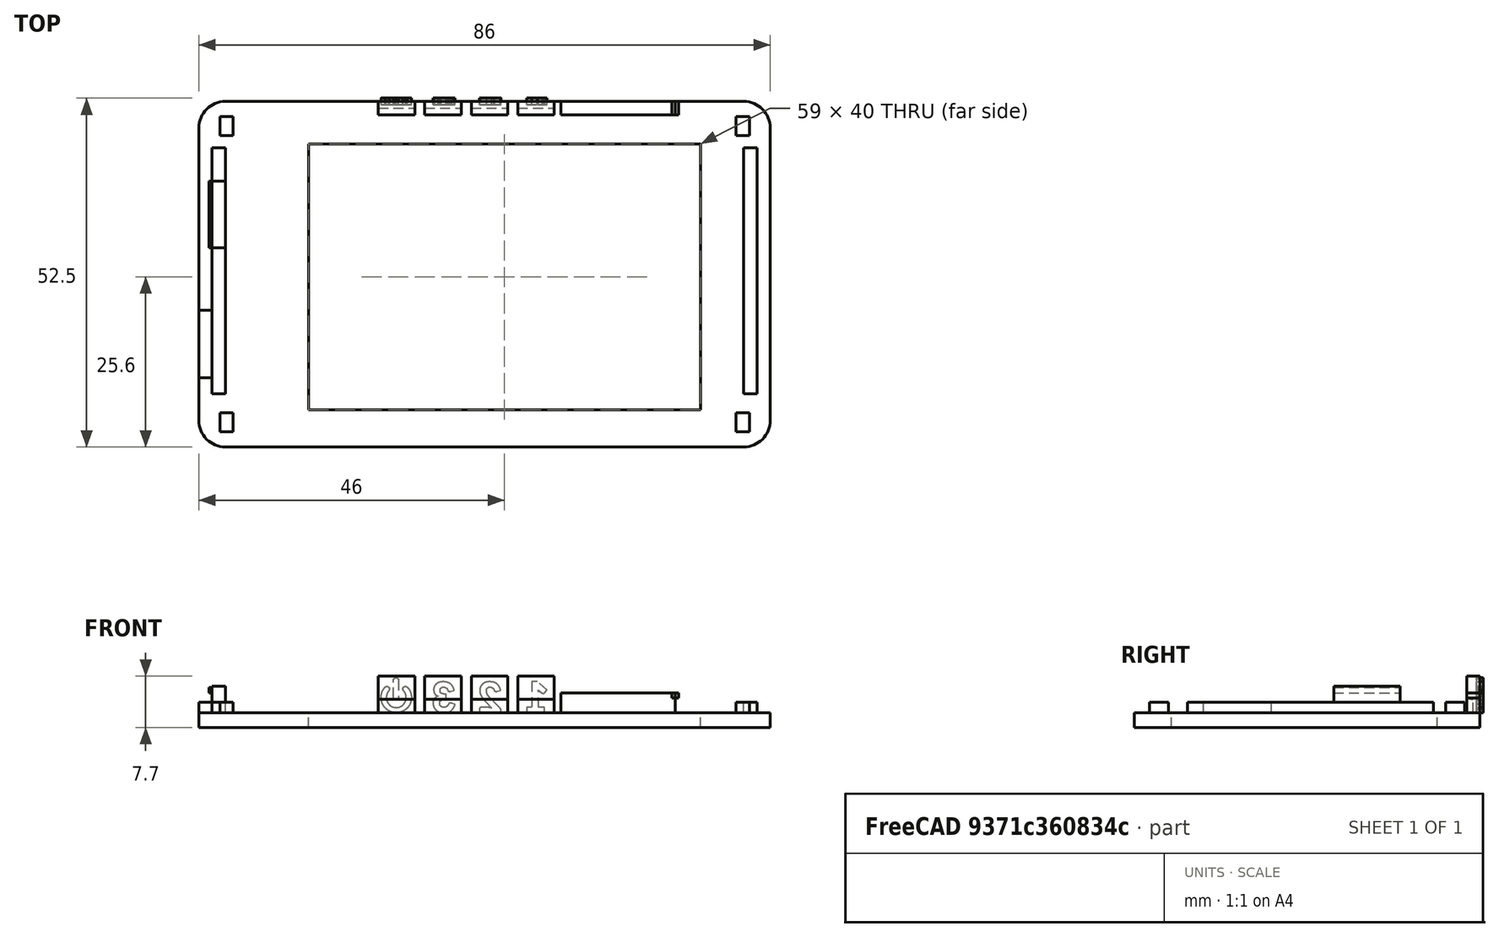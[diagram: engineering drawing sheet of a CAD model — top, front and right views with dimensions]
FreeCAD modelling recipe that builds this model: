
FCSTD DOCUMENT  (FreeCAD 0.18R4 (GitTag))
Label: Lid V4
License: All rights reserved
LicenseURL: http://en.wikipedia.org/wiki/All_rights_reserved
objects: Part::Box×21, Part::Fillet×5, Part::Cut×5, Part::Part2DObjectPython×4, Part::Extrusion×4, Mesh::Feature×1
note: 39 computed .brp shape members not serialized (recipe doc carries the construction recipe); baked Part::Feature solids carry a one-line shape summary decoded from their .brp

FEATURE [Mesh::Feature] TTGO_T5s_hanger___lid_6  label="TTGO_T5s_hanger_-_lid_6"
FEATURE [Part::Box] Box002  label="Würfel002"
  AttacherType = Attacher::AttachEngine3D
  Height = 2.2
  Length = 86
  Placement = pos=(-43,-26,-17.2) rot=(0,0,1;0rad)
  Width = 52
FEATURE [Part::Fillet] Fillet
  Base = -> Box002
  Edges = 4 edges r=4: [Edge1,Edge3,Edge5,Edge7]
FEATURE [Part::Box] Box  label="Würfel"
  AttacherType = Attacher::AttachEngine3D
  Height = 1.6
  Length = 2
  Placement = pos=(39,-18,-15) rot=(0,0,1;0rad)
  Width = 37
FEATURE [Part::Box] Box003  label="Würfel003"
  AttacherType = Attacher::AttachEngine3D
  Height = 1.6
  Length = 2
  Placement = pos=(-41,-18,-15) rot=(0,0,1;0rad)
  Width = 37
FEATURE [Part::Box] Box004  label="Würfel Cliphole"
  AttacherType = Attacher::AttachEngine3D
  Height = 2.4
  Length = 2
  Placement = pos=(-41,4,-13.4) rot=(0,0,1;0rad)
  Width = 10
FEATURE [Part::Box] Box005  label="Würfel USB"
  AttacherType = Attacher::AttachEngine3D
  Height = 1.6
  Length = 2
  Placement = pos=(-43,-15.6,-15) rot=(0,0,1;0rad)
  Width = 10.2
FEATURE [Part::Box] Box010  label="Cliphole"
  AttacherType = Attacher::AttachEngine3D
  Height = 0.8
  Length = 0.5
  Placement = pos=(-41.5,4,-12) rot=(0,0,1;0rad)
  Width = 10
FEATURE [Part::Box] Box011  label="Würfel SD"
  AttacherType = Attacher::AttachEngine3D
  Height = 3
  Length = 17.2
  Placement = pos=(11.5,24,-15) rot=(0,0,1;0rad)
  Width = 2
FEATURE [Part::Box] Box012  label="Würfel Placeholder 1"
  AttacherType = Attacher::AttachEngine3D
  Height = 1.6
  Length = 2
  Placement = pos=(37.85,20.85,-15) rot=(0,0,1;0rad)
  Width = 2.85
FEATURE [Part::Box] Box013  label="Würfel Placeholder 2"
  AttacherType = Attacher::AttachEngine3D
  Height = 1.6
  Length = 2
  Placement = pos=(-39.85,20.85,-15) rot=(0,0,1;0rad)
  Width = 2.85
FEATURE [Part::Box] Box014  label="Würfel Placeholder 3"
  AttacherType = Attacher::AttachEngine3D
  Height = 1.6
  Length = 2
  Placement = pos=(37.85,-23.7,-15) rot=(0,0,1;0rad)
  Width = 2.85
FEATURE [Part::Box] Box015  label="Würfel Placeholder 4"
  AttacherType = Attacher::AttachEngine3D
  Height = 1.6
  Length = 2
  Placement = pos=(-39.85,-23.7,-15) rot=(0,0,1;0rad)
  Width = 2.85
FEATURE [Part::Box] Box016  label="Button 1 Base"
  AttacherType = Attacher::AttachEngine3D
  Height = 5.5
  Length = 5.5
  Placement = pos=(5,24,-15) rot=(0,0,1;0rad)
  Width = 2
FEATURE [Part::Box] Box017  label="Button 1 Cut"
  AttacherType = Attacher::AttachEngine3D
  Height = 2
  Length = 5.5
  Placement = pos=(5,24,-15) rot=(0,0,1;0rad)
  Width = 1
FEATURE [Part::Cut] Cut
  Base = -> Box016
  Tool = -> Box017
FEATURE [Part::Fillet] Fillet002  label="Button 1"
  Base = -> Cut
  Edges = 1 edges r=0.9: [Edge7]
FEATURE [Part::Box] Box018  label="Button 1 Base001"
  AttacherType = Attacher::AttachEngine3D
  Height = 5.5
  Length = 5.5
  Placement = pos=(5,24,-15) rot=(0,0,1;0rad)
  Width = 2
FEATURE [Part::Box] Box019  label="Button 1 Cut001"
  AttacherType = Attacher::AttachEngine3D
  Height = 2
  Length = 5.5
  Placement = pos=(5,24,-15) rot=(0,0,1;0rad)
  Width = 1
FEATURE [Part::Cut] Cut001
  Base = -> Box018
  Tool = -> Box019
FEATURE [Part::Fillet] Fillet003  label="Button 2"
  Base = -> Cut001
  Edges = 1 edges r=0.9: [Edge7]
  Placement = pos=(-7,0,0) rot=(0,0,1;0rad)
FEATURE [Part::Box] Box020  label="Button 1 Base002"
  AttacherType = Attacher::AttachEngine3D
  Height = 5.5
  Length = 5.5
  Placement = pos=(5,24,-15) rot=(0,0,1;0rad)
  Width = 2
FEATURE [Part::Box] Box021  label="Button 1 Cut002"
  AttacherType = Attacher::AttachEngine3D
  Height = 2
  Length = 5.5
  Placement = pos=(5,24,-15) rot=(0,0,1;0rad)
  Width = 1
FEATURE [Part::Cut] Cut002
  Base = -> Box020
  Tool = -> Box021
FEATURE [Part::Fillet] Fillet004  label="Button 3"
  Base = -> Cut002
  Edges = 1 edges r=0.9: [Edge7]
  Placement = pos=(-14,0,0) rot=(0,0,1;0rad)
FEATURE [Part::Box] Box022  label="Button 1 Base003"
  AttacherType = Attacher::AttachEngine3D
  Height = 5.5
  Length = 5.5
  Placement = pos=(5,24,-15) rot=(0,0,1;0rad)
  Width = 2
FEATURE [Part::Box] Box023  label="Button 1 Cut003"
  AttacherType = Attacher::AttachEngine3D
  Height = 2
  Length = 5.5
  Placement = pos=(5,24,-15) rot=(0,0,1;0rad)
  Width = 1
FEATURE [Part::Cut] Cut003
  Base = -> Box022
  Tool = -> Box023
FEATURE [Part::Fillet] Fillet005  label="Button 4"
  Base = -> Cut003
  Edges = 1 edges r=0.9: [Edge7]
  Placement = pos=(-21,0,0) rot=(0,0,1;0rad)
FEATURE [Part::Box] Box024  label="Display Cut"
  AttacherType = Attacher::AttachEngine3D
  Height = 4
  Length = 59
  Placement = pos=(-26.5,-20.4,-18) rot=(0,0,1;0rad)
  Width = 40
FEATURE [Part::Part2DObjectPython] ShapeString  # Draft 2D object (typed FeaturePython)
  FontFile = <userpath>/Documents/3D Printer/All Fonts/Lato-Black.ttf
  Placement = pos=(0,0,0) rot=(0,0.707107,0.707107;3.14159rad)
  Size = 5
  String = 1
  Tracking = 0
FEATURE [Part::Extrusion] Extrude  label="Btn1 Extrude"
  Base = -> ShapeString
  Dir = (0,1,-2e-16)
  DirMode = 2
  FaceMakerClass = Part::FaceMakerBullseye
  LengthFwd = 1
  LengthRev = 0
  Placement = pos=(9.8,25.5,-15) rot=(0,0,1;0rad)
  Solid = false
  Symmetric = false
FEATURE [Part::Part2DObjectPython] ShapeString001  # Draft 2D object (typed FeaturePython)
  FontFile = <userpath>/Documents/3D Printer/All Fonts/Lato-Black.ttf
  Placement = pos=(0,0,0) rot=(0,0.707107,0.707107;3.14159rad)
  Size = 5
  String = 2
  Tracking = 0
FEATURE [Part::Extrusion] Extrude001  label="Btn2 Extrude"
  Base = -> ShapeString001
  Dir = (0,1,-2e-16)
  DirMode = 2
  FaceMakerClass = Part::FaceMakerBullseye
  LengthFwd = 1
  LengthRev = 0
  Placement = pos=(2.7,25.5,-15) rot=(0,0,1;0rad)
  Solid = false
  Symmetric = false
FEATURE [Part::Part2DObjectPython] ShapeString002  # Draft 2D object (typed FeaturePython)
  FontFile = <userpath>/Documents/3D Printer/All Fonts/Lato-Black.ttf
  Placement = pos=(0,0,0) rot=(0,0.707107,0.707107;3.14159rad)
  Size = 5
  String = 3
  Tracking = 0
FEATURE [Part::Extrusion] Extrude002  label="Btn3 Extrude"
  Base = -> ShapeString002
  Dir = (0,1,-2e-16)
  DirMode = 2
  FaceMakerClass = Part::FaceMakerBullseye
  LengthFwd = 1
  LengthRev = 0
  Placement = pos=(-4.2,25.5,-15) rot=(0,0,1;0rad)
  Solid = false
  Symmetric = false
FEATURE [Part::Part2DObjectPython] ShapeString003  # Draft 2D object (typed FeaturePython)
  FontFile = <userpath>/Documents/3D Printer/All Fonts/Unicode_IEC_symbol.ttf
  Placement = pos=(0,0,0) rot=(0,0.707107,0.707107;3.14159rad)
  Size = 4
  String = ⏻
  Tracking = 0
FEATURE [Part::Extrusion] Extrude003  label="Btn4 Extrude"
  Base = -> ShapeString003
  Dir = (0,1,-2e-16)
  DirMode = 2
  FaceMakerClass = Part::FaceMakerBullseye
  LengthFwd = 1
  LengthRev = 0
  Placement = pos=(-10.65,25.5,-15) rot=(0,0,1;0rad)
  Solid = false
  Symmetric = false
FEATURE [Part::Cut] Cut004  label="Main Lid"
  Base = -> Fillet
  Tool = -> Box024
FEATURE [Part::Box] Box025  label="LidHolder"
  AttacherType = Attacher::AttachEngine3D
  Height = 0.8
  Length = 1
  Placement = pos=(28.2,24,-12.8) rot=(0,0,1;0rad)
  Width = 2
